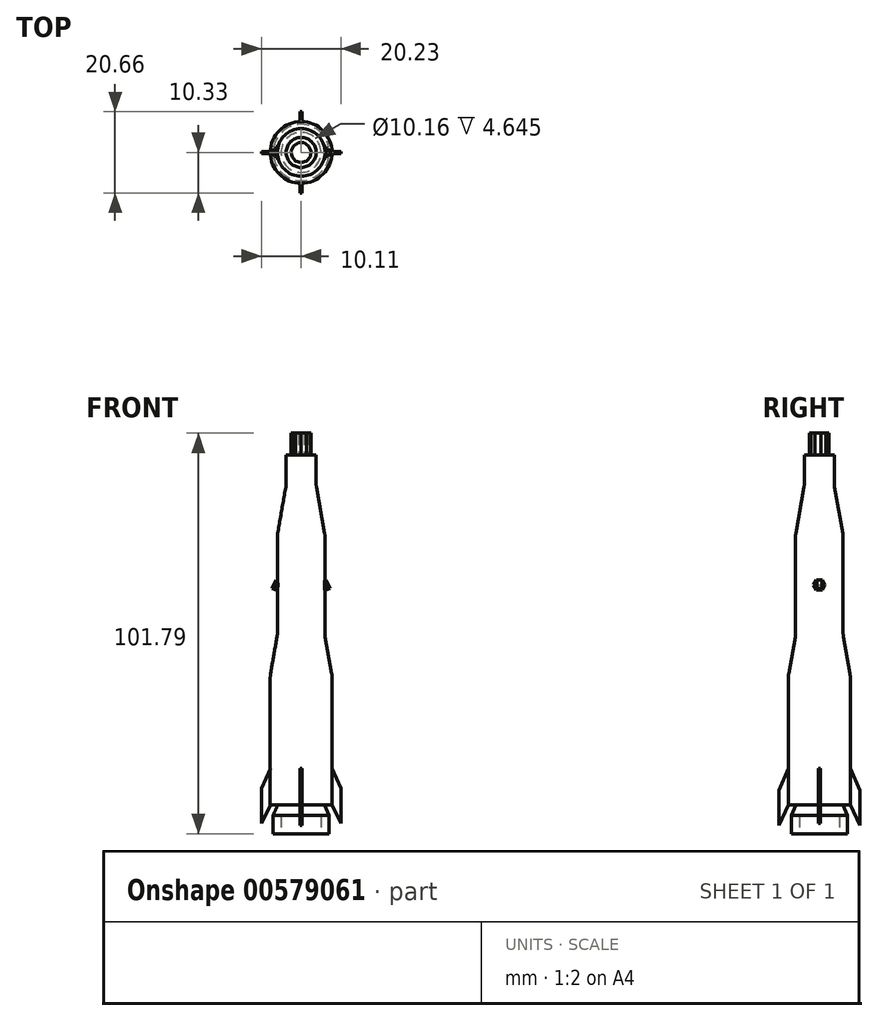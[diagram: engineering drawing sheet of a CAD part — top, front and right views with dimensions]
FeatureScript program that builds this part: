
annotation { "Feature Type Name" : "Feature", "Feature Type Description" : "" }
export const myFeature = defineFeature(function(context is Context, id is Id, definition is map)
    precondition{}
    {
        {
            var Q0;
            Q0=qCreatedBy(makeId("Front.planeOp"),FACE);
            var sketch = newSketch(context, id + "F0", { "sketchPlane" : qUnion([Q0])});
            skLineSegment(sketch, "E0", {"start": v(0, -29.86) * mm, "end": v(0, 59.04) * mm});
            skLineSegment(sketch, "E1", {"start": v(0, 59.04) * mm, "end": v(3.8, 59.04) * mm});
            skLineSegment(sketch, "E2", {"start": v(3.81, 59.04) * mm, "end": v(3.81, 51.42) * mm});
            skLineSegment(sketch, "E3", {"start": v(3.81, 51.42) * mm, "end": v(6.05, 38.72) * mm});
            skLineSegment(sketch, "E4", {"start": v(6.05, 38.72) * mm, "end": v(6.05, 13.32) * mm});
            skLineSegment(sketch, "E5", {"start": v(6.05, 13.32) * mm, "end": v(7.84, 3.16) * mm});
            skLineSegment(sketch, "E6", {"start": v(7.84, 3.16) * mm, "end": v(7.84, -29.86) * mm});
            skLineSegment(sketch, "E7", {"start": v(7.84, -29.86) * mm, "end": v(0, -29.86) * mm});
            skLineSegment(sketch, "E8", {"start": v(5.93, -29.86) * mm, "end": v(7.14, -32.46) * mm});
            skLineSegment(sketch, "E9", {"start": v(7.14, -32.46) * mm, "end": v(7.14, -37.16) * mm});
            skLineSegment(sketch, "E10", {"start": v(7.14, -37.16) * mm, "end": v(0, -37.16) * mm});
            skLineSegment(sketch, "E11", {"start": v(0, -37.16) * mm, "end": v(0, -29.86) * mm});
            skSolve(sketch);
        }
        {
            var Q0;
            Q0 = qSketchRegion(id + "F0", true);
            var Q1;
            Q1=sQuery(id+"F0.wireOp",EDGE,"E0");
            revolve(context, id + "F1", {"entities" : qUnion([Q0]), "axis" : qUnion([Q1]), "revolveType" : RevolveType.FULL});
        }
        {
            var Q0;
            Q0=qCreatedBy(makeId("Right.planeOp"),FACE);
            var sketch = newSketch(context, id + "F2", { "sketchPlane" : qUnion([Q0])});
            skLineSegment(sketch, "E12", {"start": v(-7.84, -29.86) * mm, "end": v(-7.84, 3.16) * mm});
            skLineSegment(sketch, "E13", {"start": v(7.84, 3.16) * mm, "end": v(7.84, -29.86) * mm});
            skLineSegment(sketch, "E14.0", {"start": v(7.84, -29.86) * mm, "end": v(-7.84, -29.86) * mm});
            skLineSegment(sketch, "E15", {"start": v(-7.84, -20.53) * mm, "end": v(-10.33, -26.12) * mm});
            skLineSegment(sketch, "E16", {"start": v(-10.33, -26.12) * mm, "end": v(-10.33, -35.01) * mm});
            skLineSegment(sketch, "E17", {"start": v(7.84, -20.53) * mm, "end": v(10.33, -26.12) * mm});
            skLineSegment(sketch, "E18", {"start": v(10.33, -26.12) * mm, "end": v(10.33, -35.01) * mm});
            skLineSegment(sketch, "E19", {"start": v(-10.33, -35.01) * mm, "end": v(-7.84, -29.86) * mm});
            skLineSegment(sketch, "E20", {"start": v(10.33, -35.01) * mm, "end": v(7.84, -29.86) * mm});
            skSolve(sketch);
        }
        {
            var Q0;
            {var subQ2=sQuery(id+"F2.wireOp",EDGE,"E15");Q0=makeQuery(id+"F2.imprint","IMPRINT",FACE,{"disambiguationData":[TD([[makeQuery(id+"F2.imprint","IMPRINT",EDGE,{"derivedFrom":subQ2}),1.0]])]});}
            var Q1;
            {var subQ2=sQuery(id+"F2.wireOp",EDGE,"E17");Q1=makeQuery(id+"F2.imprint","IMPRINT",FACE,{"disambiguationData":[TD([[makeQuery(id+"F2.imprint","IMPRINT",EDGE,{"derivedFrom":subQ2}),-1.0]])]});}
            extrude(context, id + "F3", {"entities" : qUnion([Q0, Q1]), "endBound" : BoundingType.SYMMETRIC, "oppositeDirection" : true, "depth" : 0.56 * mm, "offsetDistance" : 25.4 * mm});
        }
        {
            var Q0;
            Q0=qCreatedBy(makeId("Front.planeOp"),FACE);
            var sketch = newSketch(context, id + "F4", { "sketchPlane" : qUnion([Q0])});
            skLineSegment(sketch, "E21.0.0", {"start": v(0.28, -26.12) * mm, "end": v(0.28, -20.53) * mm});
            skLineSegment(sketch, "E21.0.1", {"start": v(0.28, -20.53) * mm, "end": v(-0.28, -20.53) * mm});
            skLineSegment(sketch, "E21.0.2", {"start": v(-0.28, -20.53) * mm, "end": v(-0.28, -26.12) * mm});
            skLineSegment(sketch, "E21.0.3", {"start": v(-0.28, -26.12) * mm, "end": v(0.28, -26.12) * mm});
            skLineSegment(sketch, "E22.0.0", {"start": v(0.28, -35.01) * mm, "end": v(0.28, -26.12) * mm});
            skLineSegment(sketch, "E22.0.1", {"start": v(0.28, -26.12) * mm, "end": v(-0.28, -26.12) * mm});
            skLineSegment(sketch, "E22.0.2", {"start": v(-0.28, -26.12) * mm, "end": v(-0.28, -35.01) * mm});
            skLineSegment(sketch, "E22.0.3", {"start": v(-0.28, -35.01) * mm, "end": v(0.28, -35.01) * mm});
            skLineSegment(sketch, "E23", {"start": v(-7.84, -29.86) * mm, "end": v(-7.84, 3.16) * mm});
            skLineSegment(sketch, "E24", {"start": v(7.84, 3.16) * mm, "end": v(7.84, -29.86) * mm});
            skLineSegment(sketch, "E25", {"start": v(0.28, -20.53) * mm, "end": v(7.84, -20.53) * mm, "construction": true});
            skLineSegment(sketch, "E26", {"start": v(7.84, -20.53) * mm, "end": v(10.12, -25.64) * mm});
            skLineSegment(sketch, "E27", {"start": v(10.12, -25.64) * mm, "end": v(10.12, -34.53) * mm});
            skLineSegment(sketch, "E28", {"start": v(10.12, -34.53) * mm, "end": v(7.84, -29.86) * mm});
            skLineSegment(sketch, "E29", {"start": v(-0.28, -20.53) * mm, "end": v(-7.84, -20.53) * mm, "construction": true});
            skLineSegment(sketch, "E30", {"start": v(-7.84, -20.53) * mm, "end": v(-10.11, -25.64) * mm});
            skLineSegment(sketch, "E31", {"start": v(-10.11, -25.64) * mm, "end": v(-10.11, -34.53) * mm});
            skLineSegment(sketch, "E32", {"start": v(-10.11, -34.53) * mm, "end": v(-7.84, -29.86) * mm});
            skSolve(sketch);
        }
        {
            var Q0;
            {var subQ2=sQuery(id+"F4.wireOp",EDGE,"E30");Q0=makeQuery(id+"F4.imprint","IMPRINT",FACE,{"disambiguationData":[TD([[makeQuery(id+"F4.imprint","IMPRINT",EDGE,{"derivedFrom":subQ2}),1.0]])]});}
            var Q1;
            {var subQ2=sQuery(id+"F4.wireOp",EDGE,"E26");Q1=makeQuery(id+"F4.imprint","IMPRINT",FACE,{"disambiguationData":[TD([[makeQuery(id+"F4.imprint","IMPRINT",EDGE,{"derivedFrom":subQ2}),-1.0]])]});}
            extrude(context, id + "F5", {"entities" : qUnion([Q0, Q1]), "operationType" : NewBodyOperationType.ADD, "endBound" : BoundingType.SYMMETRIC, "depth" : 0.56 * mm, "offsetDistance" : 25.4 * mm});
        }
        {
            var Q0;
            Q0=makeQuery(id+"F1.opRevolve","SWEPT_FACE",FACE,{"disambiguationData":[OSD([sQuery(id+"F0.wireOp",EDGE,"E1")])]});
            var sketch = newSketch(context, id + "F6", { "sketchPlane" : qUnion([Q0])});
            skCircle(sketch, "E33.cCircle", {"center": v(0, 0) * mm, "radius": 2.46 * mm, "construction": true});
            skLineSegment(sketch, "E33.0", {"start": v(-0.72, 2.46) * mm, "end": v(0.72, 2.46) * mm});
            skLineSegment(sketch, "E33.1", {"start": v(0.72, 2.46) * mm, "end": v(1.93, 1.68) * mm});
            skLineSegment(sketch, "E33.2", {"start": v(1.93, 1.68) * mm, "end": v(2.53, 0.36) * mm});
            skLineSegment(sketch, "E33.3", {"start": v(2.53, 0.36) * mm, "end": v(2.33, -1.06) * mm});
            skLineSegment(sketch, "E33.4", {"start": v(2.33, -1.06) * mm, "end": v(1.38, -2.15) * mm});
            skLineSegment(sketch, "E33.5", {"start": v(1.38, -2.15) * mm, "end": v(0, -2.56) * mm});
            skLineSegment(sketch, "E33.6", {"start": v(0, -2.56) * mm, "end": v(-1.38, -2.15) * mm});
            skLineSegment(sketch, "E33.7", {"start": v(-1.38, -2.15) * mm, "end": v(-2.33, -1.06) * mm});
            skLineSegment(sketch, "E33.8", {"start": v(-2.33, -1.06) * mm, "end": v(-2.53, 0.36) * mm});
            skLineSegment(sketch, "E33.9", {"start": v(-2.53, 0.36) * mm, "end": v(-1.93, 1.68) * mm});
            skLineSegment(sketch, "E33.10", {"start": v(-1.93, 1.68) * mm, "end": v(-0.72, 2.46) * mm});
            skPoint(sketch, "E33.0.midPoint", {"position": v(0, 2.46) * mm});
            skSolve(sketch);
        }
        {
            var Q0;
            Q0 = qSketchRegion(id + "F6", true);
            extrude(context, id + "F7", {"entities" : qUnion([Q0]), "operationType" : NewBodyOperationType.ADD, "depth" : 5.6 * mm, "offsetDistance" : 25.4 * mm});
        }
        {
            var Q0;
            Q0=qCreatedBy(makeId("Top.planeOp"),FACE);
            var sketch = newSketch(context, id + "F8", { "sketchPlane" : qUnion([Q0])});
            skCircle(sketch, "E34", {"center": v(0, 0) * mm, "radius": 5.08 * mm});
            skSolve(sketch);
        }
        {
            var Q0;
            Q0 = qSketchRegion(id + "F8", true);
            extrude(context, id + "F9", {"entities" : qUnion([Q0]), "operationType" : NewBodyOperationType.ADD, "oppositeDirection" : true, "depth" : 38.1 * mm, "offsetDistance" : 25.4 * mm});
        }
        {
            var Q0;
            Q0=makeQuery(id+"F1.opRevolve","SWEPT_EDGE",EDGE,{"disambiguationData":[OSD([sQuery(id+"F0.wireOp",EDGE,"E5"),sQuery(id+"F0.wireOp",EDGE,"E6")])]});
            fillet(context, id + "F10", {"entities" : qUnion([Q0]), "radius" : 5.08 * mm, "tangentPropagation" : true, "allowEdgeOverflow" : false});
        }
        {
            var Q0;
            Q0=makeQuery(id+"F1.opRevolve","SWEPT_EDGE",EDGE,{"disambiguationData":[OSD([sQuery(id+"F0.wireOp",EDGE,"E4"),sQuery(id+"F0.wireOp",EDGE,"E5")])]});
            var Q1;
            Q1=makeQuery(id+"F1.opRevolve","SWEPT_EDGE",EDGE,{"disambiguationData":[OSD([sQuery(id+"F0.wireOp",EDGE,"E3"),sQuery(id+"F0.wireOp",EDGE,"E4")])]});
            var Q2;
            Q2=makeQuery(id+"F1.opRevolve","SWEPT_EDGE",EDGE,{"disambiguationData":[OSD([sQuery(id+"F0.wireOp",EDGE,"E2"),sQuery(id+"F0.wireOp",EDGE,"E3")])]});
            fillet(context, id + "F11", {"entities" : qUnion([Q0, Q1, Q2]), "radius" : 5.08 * mm, "tangentPropagation" : true, "allowEdgeOverflow" : false});
        }
        {
            var Q0;
            Q0=makeQuery(id+"F9.opExtrude","CAP_FACE",FACE,{"disambiguationData":[OSD([sQuery(id+"F8.wireOp",EDGE,"E34")])],"isStart":false});
            extrude(context, id + "F12", {"entities" : qUnion([Q0]), "operationType" : NewBodyOperationType.REMOVE, "oppositeDirection" : true, "depth" : 5.6 * mm, "offsetDistance" : 25.4 * mm});
        }
        {
            var Q0;
            Q0=qCreatedBy(makeId("Right.planeOp"),FACE);
            var sketch = newSketch(context, id + "F13", { "sketchPlane" : qUnion([Q0])});
            skLineSegment(sketch, "E35", {"start": v(-6.05, 13.76) * mm, "end": v(-6.05, 38.28) * mm});
            skLineSegment(sketch, "E36", {"start": v(6.05, 38.28) * mm, "end": v(6.05, 13.76) * mm});
            skLineSegment(sketch, "E37", {"start": v(-6.05, 26.02) * mm, "end": v(6.05, 26.02) * mm});
            skPoint(sketch, "E38.startSnap0", {"position": v(0, 26.02) * mm});
            skLineSegment(sketch, "E39", {"start": v(0, 26.02) * mm, "end": v(0, 27.3) * mm});
            skLineSegment(sketch, "E40", {"start": v(0, 26.02) * mm, "end": v(0, 24.75) * mm});
            skCircle(sketch, "E41.cCircle", {"center": v(0, 26.02) * mm, "radius": 1.27 * mm, "construction": true});
            skLineSegment(sketch, "E41.0", {"start": v(-0.74, 27.3) * mm, "end": v(0.74, 27.3) * mm});
            skLineSegment(sketch, "E41.1", {"start": v(0.74, 27.3) * mm, "end": v(1.47, 26.02) * mm});
            skLineSegment(sketch, "E41.2", {"start": v(1.47, 26.02) * mm, "end": v(0.74, 24.75) * mm});
            skLineSegment(sketch, "E41.3", {"start": v(0.74, 24.75) * mm, "end": v(-0.74, 24.75) * mm});
            skLineSegment(sketch, "E41.4", {"start": v(-0.74, 24.75) * mm, "end": v(-1.47, 26.02) * mm});
            skLineSegment(sketch, "E41.5", {"start": v(-1.47, 26.02) * mm, "end": v(-0.74, 27.3) * mm});
            skPoint(sketch, "E41.0.midPoint", {"position": v(0, 27.3) * mm});
            skSolve(sketch);
        }
        {
            var Q0;
            Q0 = qSketchRegion(id + "F13", true);
            extrude(context, id + "F14", {"entities" : qUnion([Q0]), "operationType" : NewBodyOperationType.ADD, "endBound" : BoundingType.SYMMETRIC, "depth" : 12.7 * mm, "offsetDistance" : 25.4 * mm});
        }
        {
            var Q0;
            Q0=qCreatedBy(makeId("Front.planeOp"),FACE);
            var sketch = newSketch(context, id + "F15", { "sketchPlane" : qUnion([Q0])});
            skEllipticalArc(sketch, "E42.0.0", {});
            skLineSegment(sketch, "E42.0.1", {"start": v(5.87, 26.02) * mm, "end": v(6.35, 26.02) * mm});
            skLineSegment(sketch, "E42.0.2", {"start": v(6.35, 26.02) * mm, "end": v(6.35, 27.3) * mm});
            skLineSegment(sketch, "E42.0.3", {"start": v(6.35, 27.3) * mm, "end": v(6, 27.3) * mm});
            skEllipticalArc(sketch, "E43.0.0", {});
            skLineSegment(sketch, "E43.0.1", {"start": v(6, 24.75) * mm, "end": v(6.35, 24.75) * mm});
            skLineSegment(sketch, "E43.0.2", {"start": v(6.35, 24.75) * mm, "end": v(6.35, 26.02) * mm});
            skLineSegment(sketch, "E43.0.3", {"start": v(6.35, 26.02) * mm, "end": v(5.87, 26.02) * mm});
            skEllipticalArc(sketch, "E44.0.0", {});
            skLineSegment(sketch, "E44.0.1", {"start": v(-6, 27.3) * mm, "end": v(-6.35, 27.3) * mm});
            skLineSegment(sketch, "E44.0.2", {"start": v(-6.35, 27.3) * mm, "end": v(-6.35, 26.02) * mm});
            skLineSegment(sketch, "E44.0.3", {"start": v(-6.35, 26.02) * mm, "end": v(-5.87, 26.02) * mm});
            skEllipticalArc(sketch, "E45.0.0", {});
            skLineSegment(sketch, "E45.0.1", {"start": v(-5.87, 26.02) * mm, "end": v(-6.35, 26.02) * mm});
            skLineSegment(sketch, "E45.0.2", {"start": v(-6.35, 26.02) * mm, "end": v(-6.35, 24.75) * mm});
            skLineSegment(sketch, "E45.0.3", {"start": v(-6.35, 24.75) * mm, "end": v(-6, 24.75) * mm});
            skLineSegment(sketch, "E46", {"start": v(6.35, 27.3) * mm, "end": v(7.36, 25.2) * mm});
            skLineSegment(sketch, "E47", {"start": v(7.36, 25.2) * mm, "end": v(6.35, 24.75) * mm});
            skLineSegment(sketch, "E48", {"start": v(-6.35, 27.3) * mm, "end": v(-7.36, 25.19) * mm});
            skLineSegment(sketch, "E49", {"start": v(-6.35, 24.75) * mm, "end": v(-7.36, 25.19) * mm});
            const initialGuessF15  = {"E42.0.0": [0, 0.028566845012805007, 0, -1, 0.010477786151357365, 0.006049352654997511, 1.3252868937246787, 1.4489699425564848], "E43.0.0": [0, 0.02347358240753073, 0, -1, 0.010477786151357357, 0.006049352654997509, 1.6926227110333083, 1.816305759865115], "E44.0.0": [0, 0.028566845012805007, 0, -1, 0.010477786151357365, 0.006049352654997511, 4.834215364623102, 4.957898413454906], "E45.0.0": [0, 0.02347358240753073, 0, -1, 0.010477786151357357, 0.006049352654997509, 4.466879547314472, 4.5905625961462775]};
            skSetInitialGuess(sketch, initialGuessF15);
            skSolve(sketch);
        }
        {
            var Q0;
            Q0 = qSketchRegion(id + "F15", true);
            extrude(context, id + "F16", {"entities" : qUnion([Q0]), "endBound" : BoundingType.SYMMETRIC, "depth" : 1.27 * mm, "offsetDistance" : 25.4 * mm});
        }
    });
